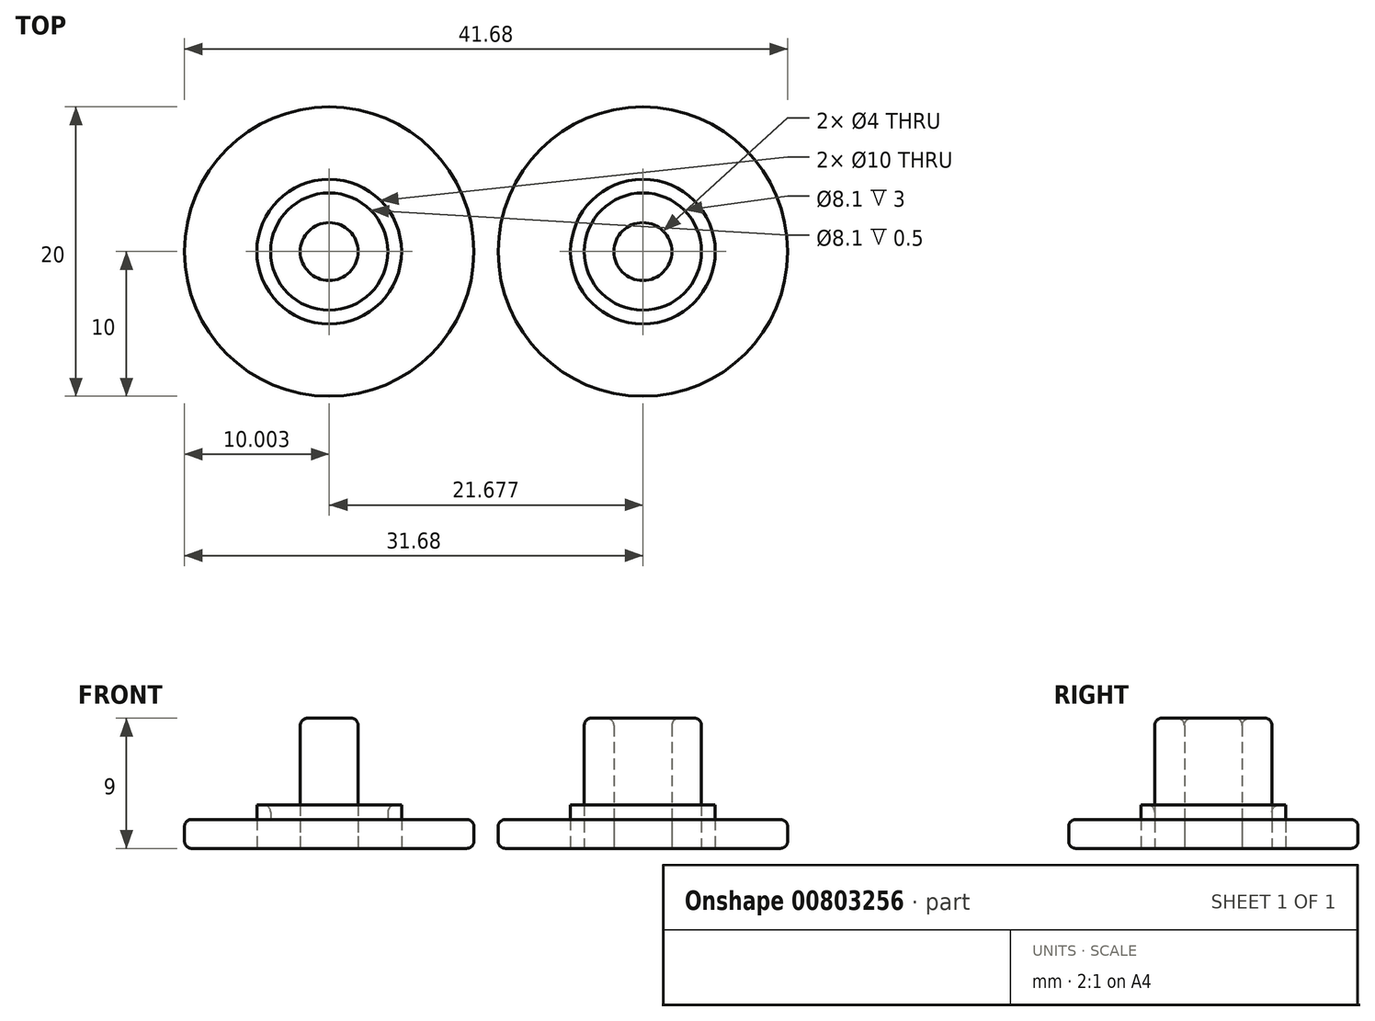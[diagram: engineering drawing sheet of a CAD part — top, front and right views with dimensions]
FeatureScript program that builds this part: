
annotation { "Feature Type Name" : "Feature", "Feature Type Description" : "" }
export const myFeature = defineFeature(function(context is Context, id is Id, definition is map)
    precondition{}
    {
        {
            var Q0;
            Q0=qCreatedBy(makeId("Top.planeOp"),FACE);
            var sketch = newSketch(context, id + "F0", { "sketchPlane" : qUnion([Q0])});
            skCircle(sketch, "E0", {"center": v(0, 0) * mm, "radius": 10 * mm});
            skCircle(sketch, "E1", {"center": v(0, 0) * mm, "radius": 4.05 * mm});
            skCircle(sketch, "E2", {"center": v(0, 0) * mm, "radius": 2 * mm});
            skCircle(sketch, "E3", {"center": v(0, 0) * mm, "radius": 5 * mm});
            skSolve(sketch);
        }
        {
            var Q0;
            Q0=qCreatedBy(makeId("Top.planeOp"),FACE);
            var sketch = newSketch(context, id + "F1", { "sketchPlane" : qUnion([Q0])});
            skCircle(sketch, "E4", {"center": v(-21.68, 0) * mm, "radius": 10 * mm});
            skCircle(sketch, "E5", {"center": v(-21.68, 0) * mm, "radius": 4.05 * mm});
            skCircle(sketch, "E6", {"center": v(-21.68, 0) * mm, "radius": 2 * mm});
            skCircle(sketch, "E7", {"center": v(-21.68, 0) * mm, "radius": 5 * mm});
            skSolve(sketch);
        }
        {
            var Q0;
            Q0=makeQuery(id+"F1.imprint","IMPRINT",FACE,{"disambiguationData":[TD([[makeQuery(id+"F1.imprint","IMPRINT",EDGE,{"derivedFrom":sQuery(id+"F1.wireOp",EDGE,"E4")}),1.0]])]});
            var Q1;
            Q1=makeQuery(id+"F0.imprint","IMPRINT",FACE,{"disambiguationData":[TD([[makeQuery(id+"F0.imprint","IMPRINT",EDGE,{"derivedFrom":sQuery(id+"F0.wireOp",EDGE,"E0")}),1.0]])]});
            extrude(context, id + "F2", {"entities" : qUnion([Q0, Q1]), "depth" : 2 * mm, "offsetDistance" : 25 * mm});
        }
        {
            var Q0;
            Q0=makeQuery(id+"F0.imprint","IMPRINT",FACE,{"disambiguationData":[TD([[makeQuery(id+"F0.imprint","IMPRINT",EDGE,{"derivedFrom":sQuery(id+"F0.wireOp",EDGE,"E1")}),-1.0]])]});
            var Q1;
            Q1=makeQuery(id+"F1.imprint","IMPRINT",FACE,{"disambiguationData":[TD([[makeQuery(id+"F1.imprint","IMPRINT",EDGE,{"derivedFrom":sQuery(id+"F1.wireOp",EDGE,"E5")}),-1.0]])]});
            extrude(context, id + "F3", {"entities" : qUnion([Q0, Q1]), "depth" : 3 * mm, "offsetDistance" : 25 * mm});
        }
        {
            var Q0;
            Q0=makeQuery(id+"F1.imprint","IMPRINT",FACE,{"disambiguationData":[TD([[makeQuery(id+"F1.imprint","IMPRINT",EDGE,{"derivedFrom":sQuery(id+"F1.wireOp",EDGE,"E5")}),1.0]])]});
            var Q1;
            Q1=makeQuery(id+"F0.imprint","IMPRINT",FACE,{"disambiguationData":[TD([[makeQuery(id+"F0.imprint","IMPRINT",EDGE,{"derivedFrom":sQuery(id+"F0.wireOp",EDGE,"E2")}),1.0]])]});
            extrude(context, id + "F4", {"entities" : qUnion([Q0, Q1]), "operationType" : NewBodyOperationType.ADD, "depth" : 2 * mm, "offsetDistance" : 25 * mm});
        }
        {
            var Q0;
            Q0=makeQuery(id+"F0.imprint","IMPRINT",FACE,{"disambiguationData":[TD([[makeQuery(id+"F0.imprint","IMPRINT",EDGE,{"derivedFrom":sQuery(id+"F0.wireOp",EDGE,"E1")}),1.0]])]});
            var Q1;
            Q1=makeQuery(id+"F1.imprint","IMPRINT",FACE,{"disambiguationData":[TD([[makeQuery(id+"F1.imprint","IMPRINT",EDGE,{"derivedFrom":sQuery(id+"F1.wireOp",EDGE,"E6")}),1.0]])]});
            extrude(context, id + "F5", {"entities" : qUnion([Q0, Q1]), "depth" : 9 * mm, "offsetDistance" : 25 * mm});
        }
        {
            var Q0;
            Q0=makeQuery(id+"F2.opExtrude","CAP_EDGE",EDGE,{"disambiguationData":[OSD([sQuery(id+"F1.wireOp",EDGE,"E4")])],"isStart":false});
            var Q1;
            Q1=makeQuery(id+"F2.opExtrude","CAP_EDGE",EDGE,{"disambiguationData":[OSD([sQuery(id+"F0.wireOp",EDGE,"E0")])],"isStart":false});
            var Q2;
            Q2=makeQuery(id+"F5.opExtrude","CAP_EDGE",EDGE,{"disambiguationData":[OSD([sQuery(id+"F0.wireOp",EDGE,"E2")])],"isStart":false});
            var Q3;
            Q3=makeQuery(id+"F5.opExtrude","CAP_EDGE",EDGE,{"disambiguationData":[OSD([sQuery(id+"F1.wireOp",EDGE,"E6")])],"isStart":false});
            var Q4;
            Q4=makeQuery(id+"F2.opExtrude","CAP_EDGE",EDGE,{"disambiguationData":[OSD([sQuery(id+"F0.wireOp",EDGE,"E0")])],"isStart":true});
            var Q5;
            Q5=makeQuery(id+"F2.opExtrude","CAP_EDGE",EDGE,{"disambiguationData":[OSD([sQuery(id+"F1.wireOp",EDGE,"E4")])],"isStart":true});
            var Q6;
            Q6=makeQuery(id+"F3.opExtrude","CAP_EDGE",EDGE,{"disambiguationData":[OSD([sQuery(id+"F1.wireOp",EDGE,"E5")])],"isStart":false});
            var Q7;
            Q7=makeQuery(id+"F5.opExtrude","CAP_EDGE",EDGE,{"disambiguationData":[OSD([sQuery(id+"F0.wireOp",EDGE,"E1")])],"isStart":false});
            fillet(context, id + "F6", {"entities" : qUnion([Q0, Q1, Q2, Q3, Q4, Q5, Q6, Q7]), "radius" : .5 * mm, "tangentPropagation" : true, "allowEdgeOverflow" : false});
        }
    });
